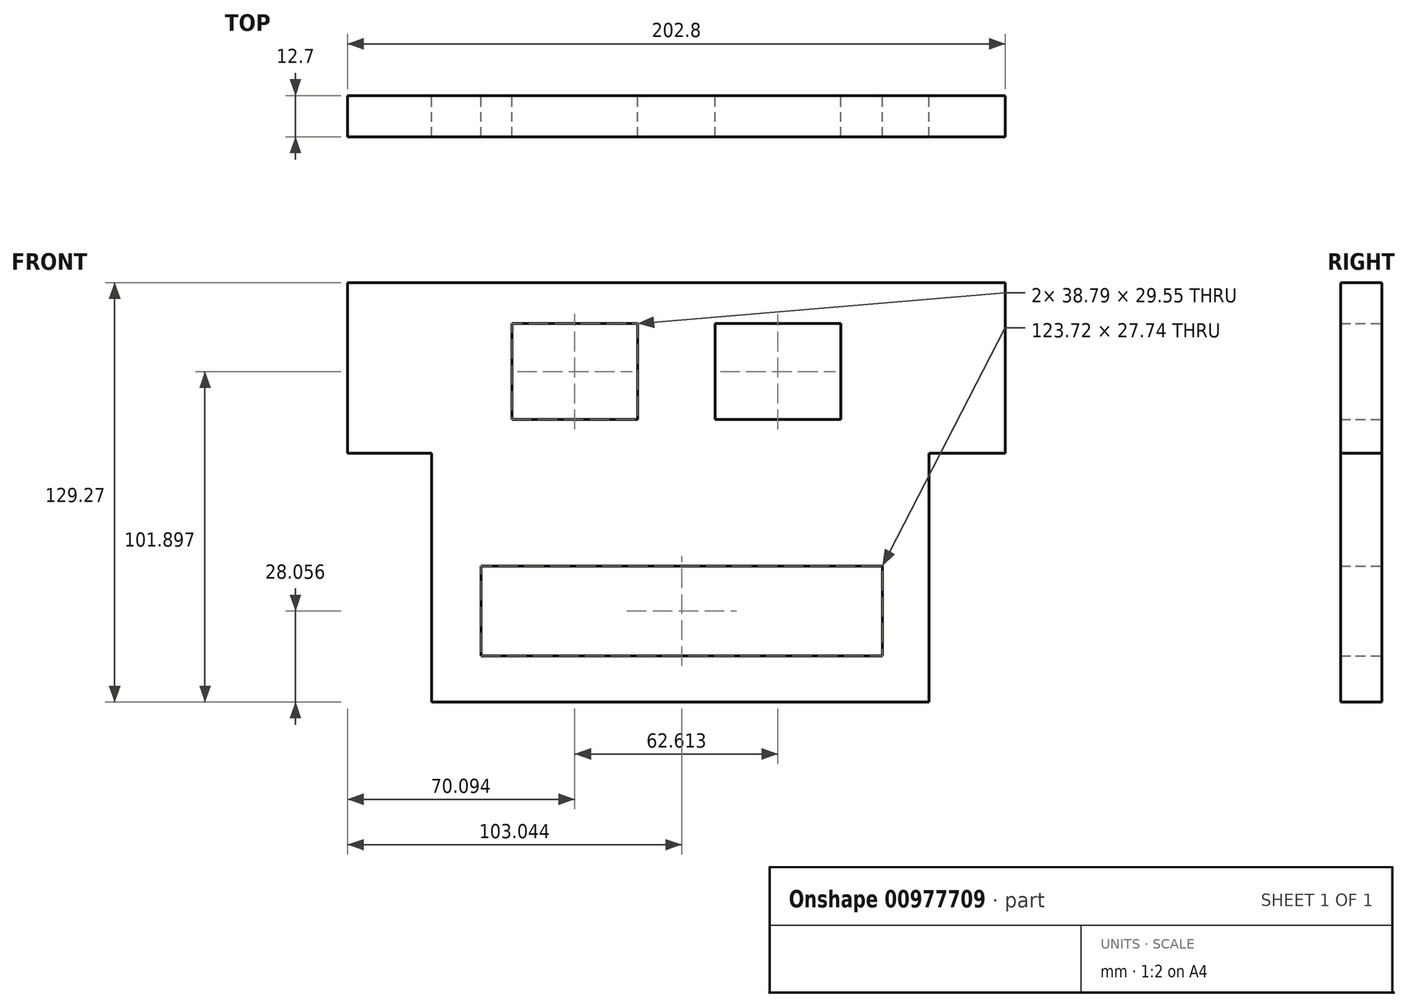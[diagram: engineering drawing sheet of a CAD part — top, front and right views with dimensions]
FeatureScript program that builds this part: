
annotation { "Feature Type Name" : "Feature", "Feature Type Description" : "" }
export const myFeature = defineFeature(function(context is Context, id is Id, definition is map)
    precondition{}
    {
        {
            var Q0;
            Q0=qCreatedBy(makeId("Front.planeOp"),FACE);
            var sketch = newSketch(context, id + "F0", { "sketchPlane" : qUnion([Q0])});
            skLineSegment(sketch, "E0.bottom", {"start": v(0, 0) * mm, "end": v(-101.4, 0) * mm});
            skLineSegment(sketch, "E0.top", {"start": v(0, 52.6) * mm, "end": v(-101.4, 52.6) * mm});
            skLineSegment(sketch, "E0.left", {"start": v(0, 0) * mm, "end": v(0, 52.6) * mm});
            skLineSegment(sketch, "E0.right", {"start": v(-101.4, 0) * mm, "end": v(-101.4, 52.6) * mm});
            skPoint(sketch, "E1.firstSnap0", {"position": v(-50.7, 52.6) * mm});
            skLineSegment(sketch, "E1.bottom", {"start": v(-50.7, 10.46) * mm, "end": v(-11.91, 10.46) * mm});
            skLineSegment(sketch, "E1.top", {"start": v(-50.7, 40.01) * mm, "end": v(-11.91, 40.01) * mm});
            skLineSegment(sketch, "E1.left", {"start": v(-50.7, 10.46) * mm, "end": v(-50.7, 40.01) * mm});
            skLineSegment(sketch, "E1.right", {"start": v(-11.91, 10.46) * mm, "end": v(-11.91, 40.01) * mm});
            skSolve(sketch);
        }
        {
            var Q0;
            Q0=makeQuery(id+"F0.imprint","IMPRINT",FACE,{"disambiguationData":[TD([[makeQuery(id+"F0.imprint","IMPRINT",EDGE,{"derivedFrom":sQuery(id+"F0.wireOp",EDGE,"E0.bottom")}),-1.0]])]});
            extrude(context, id + "F1", {"entities" : qUnion([Q0]), "depth" : 12.7 * mm, "offsetDistance" : 25.4 * mm});
        }
        {
            var Q0;
            Q0=makeQuery(id+"F1.opExtrude","SWEPT_BODY",BODY,{"disambiguationData":[OSD([sQuery(id+"F0.wireOp",EDGE,"E0.bottom"),sQuery(id+"F0.wireOp",EDGE,"E0.top"),sQuery(id+"F0.wireOp",EDGE,"E0.left"),sQuery(id+"F0.wireOp",EDGE,"E0.right"),sQuery(id+"F0.wireOp",EDGE,"E1.bottom"),sQuery(id+"F0.wireOp",EDGE,"E1.top"),sQuery(id+"F0.wireOp",EDGE,"E1.left"),sQuery(id+"F0.wireOp",EDGE,"E1.right")])]});
            var Q1;
            Q1=qCreatedBy(makeId("Right.planeOp"),FACE);
            mirror(context, id + "F2", {"operationType" : NewBodyOperationType.ADD, "entities" : qUnion([Q0]), "mirrorPlane" : qUnion([Q1])});
        }
        {
            var Q0;
            Q0=qCreatedBy(makeId("Front.planeOp"),FACE);
            var sketch = newSketch(context, id + "F3", { "sketchPlane" : qUnion([Q0])});
            skLineSegment(sketch, "E2.bottom", {"start": v(-75.42, 0) * mm, "end": v(77.83, 0) * mm});
            skLineSegment(sketch, "E2.top", {"start": v(-75.42, -76.66) * mm, "end": v(77.83, -76.66) * mm});
            skLineSegment(sketch, "E2.left", {"start": v(-75.42, 0) * mm, "end": v(-75.42, -76.66) * mm});
            skLineSegment(sketch, "E2.right", {"start": v(77.83, 0) * mm, "end": v(77.83, -76.66) * mm});
            skLineSegment(sketch, "E3.bottom", {"start": v(-60.22, -34.73) * mm, "end": v(63.5, -34.73) * mm});
            skLineSegment(sketch, "E3.top", {"start": v(-60.22, -62.48) * mm, "end": v(63.5, -62.48) * mm});
            skLineSegment(sketch, "E3.left", {"start": v(-60.22, -34.73) * mm, "end": v(-60.22, -62.48) * mm});
            skLineSegment(sketch, "E3.right", {"start": v(63.5, -34.73) * mm, "end": v(63.5, -62.48) * mm});
            skSolve(sketch);
        }
        {
            var Q0;
            Q0 = qSketchRegion(id + "F3", true);
            extrude(context, id + "F4", {"entities" : qUnion([Q0]), "operationType" : NewBodyOperationType.ADD, "depth" : 12.7 * mm, "offsetDistance" : 25.4 * mm});
        }
        {
            var Q0;
            Q0=qCreatedBy(makeId("Top.planeOp"),FACE);
            var sketch = newSketch(context, id + "F5", { "sketchPlane" : qUnion([Q0])});
            skArc(sketch, "E4", {"start": v(75.76, 0) * mm, "mid": v(0, 75.76) * mm, "end": v(-75.76, 0) * mm});
            skLineSegment(sketch, "E5", {"start": v(-75.76, 0) * mm, "end": v(75.76, 0) * mm, "construction": true});
            skSolve(sketch);
        }
        {
            var Q0;
            Q0=sQuery(id+"F5.wireOp",EDGE,"E4");
            extrude(context, id + "F6", {"bodyType" : ToolBodyType.SURFACE, "surfaceEntities" : qUnion([Q0]), "depth" : 50.8 * mm, "offsetDistance" : 25.4 * mm});
        }
    });
